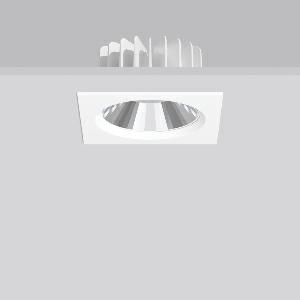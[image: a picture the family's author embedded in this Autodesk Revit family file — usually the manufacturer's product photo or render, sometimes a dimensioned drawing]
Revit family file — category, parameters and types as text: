
# Revit family: ledona_square_ip20_901533_002_2_76_a6f7
name_source: partatom
category: Lighting Fixtures
units: mm (PartAtom-declared; Revit-internal decimal feet)

## family parameters
Cut with Voids When Loaded = No
Host = Face
Light Source = No
Part Type = Normal
Room Calculation Point = No
Round Connector Dimension = Use Diameter
Shared = No

## types (1)
- TuneableWhite 846 (1 x LED Modul 846, 2600 lm, 4600)
    Apparent Load = 30 VA
    CIE Flux Codes = 89 100 100 100 100
    Color Rendering = 80
    Color Temperature = 4600
    Default Elevation = 1800 mm
    Description = Series: LEDONA square
Recessed LED downlight featuring advanced technology and sophisticated design. Housing: die-cast aluminium constructed as heat sink. Square cover plate: die-cast aluminium, powder coated. Round ceiling cut-out also with square types. Tunable white dynamically adjustable from 2700 K to 6500 K. Installation without tools thanks to spring fastening system. With connected DALI DT8 driver in separate box. With connecting cable (L 250 mm). Through-wiring box (5 pole) available as accessory. 
Colour: white
Length: 170 mm
Width: 170 mm
Height: 3 mm
Cut-out diameter: 160 mm
Recess height: 89 mm
Luminaire: recess height: 89 mm
Lamp: LED
Socket: without socket
Colour temperature: 2700K - 6500K
Colour rendering index (CRI): 80
System power: 30 W
Rated luminous flux: 2600 lm
Luminous efficiency: 87 lm/W
System power 2: 30 W
Rated luminous flux 2: 2600 lm
Luminous efficiency 2: 87 lm/W
System power 3: 31 W
Rated luminous flux 3: 2350 lm
Luminous efficiency 3: 76 lm/W
Control gear: Converter, dimmable, DALI
Protection class: II
Type of protection: IP 20
    Height = 0 mm  [stored 0 ft]
    Lamp = 1 x LED Modul 846
    Lamp Light Flux = 2600 lm
    Lamp count = 1
    Length = 170 mm  [stored 0.557743 ft]
    Lifetime = 50000 h
    Luminous efficacy = 87 lm/W
    Manufacturer = RZB
    ModVariant = No
    Model = 901533.002.2.76
    Mounting Place = Ceiling
    Mounting Type = Recessed
    Number of Poles = 1
    OnlyDefault = Yes
    Power Factor = 1
    Product Name = LEDONA square IP20
    Product group = Recessed downlights
    ProductGroupID = 402
    Protection Class = Protection class II
    Protection Degree = IP 20
    RLX_Detail_Level = 1
    RLX_Emergency_Light_Flux = 0 lm
    RLX_Emergency_Type = 0
    RLX_Emergency_Type_DB = No
    RlxData = <blob elided: 34201 chars, md5=6976ff5b>
    Socket = socket
    Standby Power = 0 W
    System Light Flux = 2600 lm
    System Power = 30 W
    Type Comments = TuneableWhite 846
    Type Image = 901391.002.jpg
    URL = http://relux.com
    VarID = tuneablewhite_846
    Voltage = 230 V
    Voltage Range = 220-240 V
    Weight = 0.00 kg
    Width = 170 mm  [stored 0.557743 ft]

note: [stored X ft] marks values corroborated as IEEE doubles in the binary element streams (Revit-internal decimal feet)

## geometry (parser evidence)
native form markers: Blend x4, Sweep x10
no freeform markers — native parametric forms only
